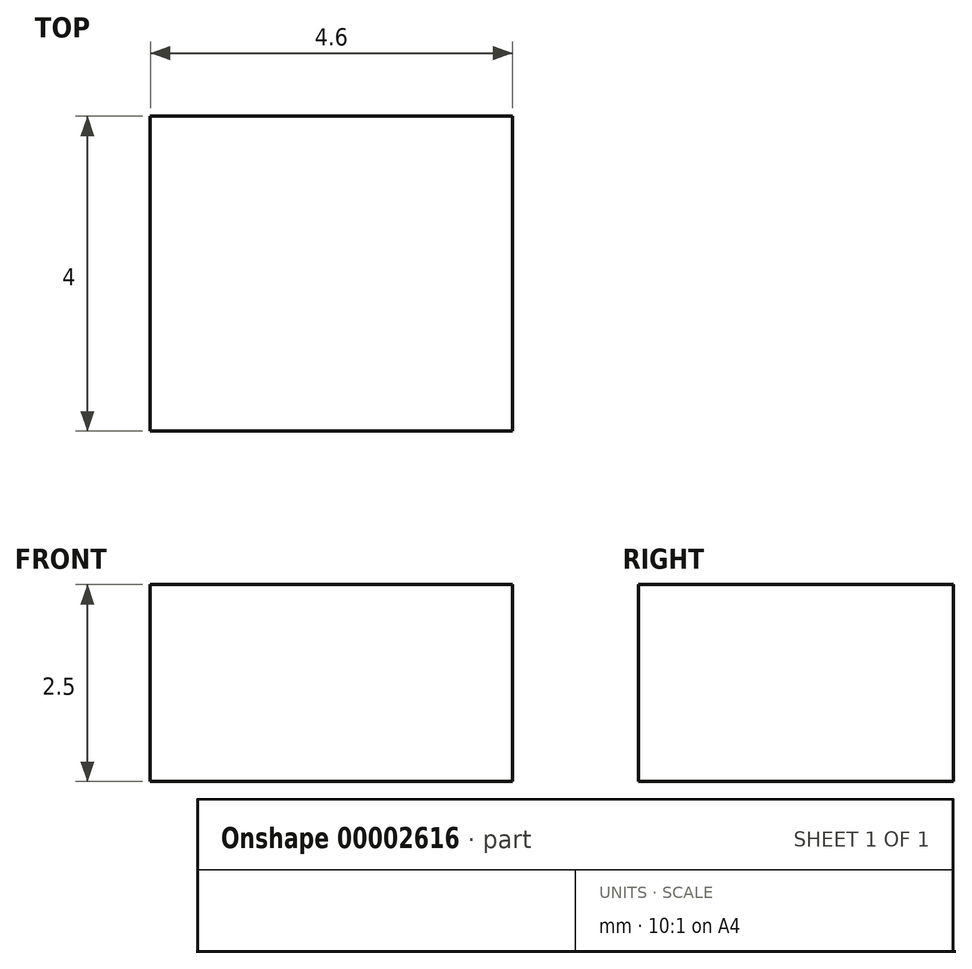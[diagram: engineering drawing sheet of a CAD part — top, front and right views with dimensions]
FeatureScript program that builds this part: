
annotation { "Feature Type Name" : "Feature", "Feature Type Description" : "" }
export const myFeature = defineFeature(function(context is Context, id is Id, definition is map)
    precondition{}
    {
        {
            var Q0;
            Q0=qCreatedBy(makeId("Top.planeOp"),FACE);
            var sketch = newSketch(context, id + "F0", { "sketchPlane" : qUnion([Q0])});
            skLineSegment(sketch, "E0.bottom", {"start": v(-2.11, 3.35) * mm, "end": v(2.49, 3.35) * mm});
            skLineSegment(sketch, "E0.top", {"start": v(-2.11, -0.65) * mm, "end": v(2.49, -0.65) * mm});
            skLineSegment(sketch, "E0.left", {"start": v(-2.11, 3.35) * mm, "end": v(-2.11, -0.65) * mm});
            skLineSegment(sketch, "E0.right", {"start": v(2.49, 3.35) * mm, "end": v(2.49, -0.65) * mm});
            skSolve(sketch);
        }
        {
            var Q0;
            Q0=makeQuery(id+"F0.imprint","IMPRINT",FACE,{"disambiguationData":[TD([[makeQuery(id+"F0.imprint","IMPRINT",EDGE,{"derivedFrom":sQuery(id+"F0.wireOp",EDGE,"E0.bottom")}),-1.0]])]});
            extrude(context, id + "F1", {"entities" : qUnion([Q0]), "depth" : 2.5 * mm});
        }
    });
